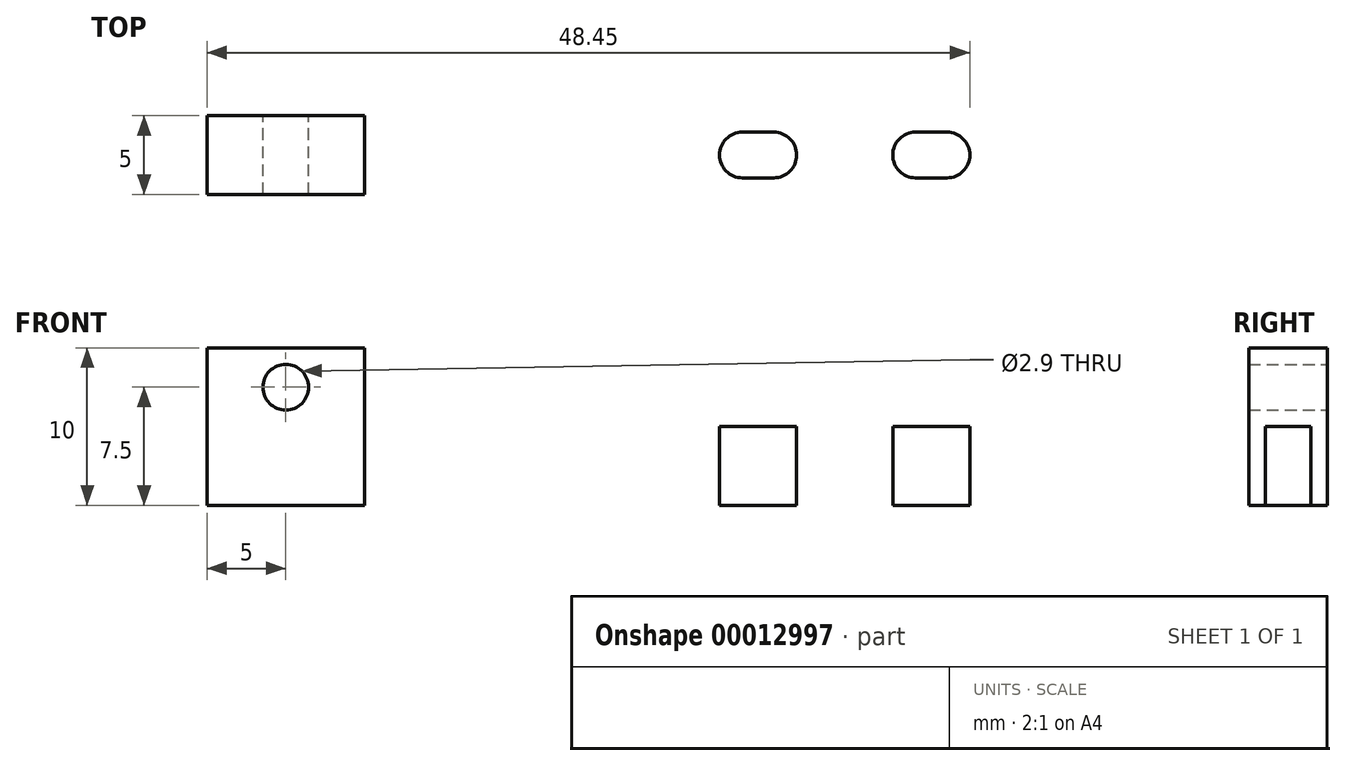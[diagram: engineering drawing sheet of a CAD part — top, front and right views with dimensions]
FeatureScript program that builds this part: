
annotation { "Feature Type Name" : "Feature", "Feature Type Description" : "" }
export const myFeature = defineFeature(function(context is Context, id is Id, definition is map)
    precondition{}
    {
        {
            var Q0;
            Q0=qCreatedBy(makeId("Top.planeOp"),FACE);
            var sketch = newSketch(context, id + "F0", { "sketchPlane" : qUnion([Q0])});
            skLineSegment(sketch, "E0.top", {"start": v(0, 7) * mm, "end": v(50, 7) * mm});
            skLineSegment(sketch, "E0.left", {"start": v(0, 0) * mm, "end": v(0, 7) * mm});
            skLineSegment(sketch, "E1", {"start": v(0, 0) * mm, "end": v(15, 0) * mm});
            skLineSegment(sketch, "E2", {"start": v(15, 0) * mm, "end": v(15, 2) * mm});
            skLineSegment(sketch, "E3", {"start": v(15, 2) * mm, "end": v(50, 2) * mm});
            skLineSegment(sketch, "E4", {"start": v(50, 2) * mm, "end": v(50, 7) * mm});
            skLineSegment(sketch, "E5.bottom", {"start": v(50, 7) * mm, "end": v(25, 7) * mm});
            skLineSegment(sketch, "E5.top", {"start": v(50, 9) * mm, "end": v(25, 9) * mm});
            skLineSegment(sketch, "E5.left", {"start": v(50, 7) * mm, "end": v(50, 9) * mm});
            skLineSegment(sketch, "E5.right", {"start": v(25, 7) * mm, "end": v(25, 9) * mm});
            skSolve(sketch);
        }
        {
            var Q0;
            Q0=makeQuery(id+"F0.imprint","IMPRINT",FACE,{"disambiguationData":[TD([[makeQuery(id+"F0.imprint","IMPRINT",EDGE,{"derivedFrom":sQuery(id+"F0.wireOp",EDGE,"E0.top")}),-1.0]])]});
            extrude(context, id + "F1", {"entities" : qUnion([Q0]), "depth" : 5 * mm});
        }
        {
            var Q0;
            Q0=makeQuery(id+"F1.opExtrude","CAP_FACE",FACE,{"disambiguationData":[OSD([sQuery(id+"F0.wireOp",EDGE,"E0.bottom"),sQuery(id+"F0.wireOp",EDGE,"E0.top"),sQuery(id+"F0.wireOp",EDGE,"E0.left"),sQuery(id+"F0.wireOp",EDGE,"E0.right")])],"isStart":false});
            var sketch = newSketch(context, id + "F2", { "sketchPlane" : qUnion([Q0])});
            skLineSegment(sketch, "E6.bottom", {"start": v(0, 7) * mm, "end": v(10, 7) * mm});
            skLineSegment(sketch, "E6.top", {"start": v(0, 2) * mm, "end": v(10, 2) * mm});
            skLineSegment(sketch, "E6.left", {"start": v(0, 7) * mm, "end": v(0, 2) * mm});
            skLineSegment(sketch, "E6.right", {"start": v(10, 7) * mm, "end": v(10, 2) * mm});
            skSolve(sketch);
        }
        {
            var Q0;
            Q0=makeQuery(id+"F2.imprint","IMPRINT",FACE,{"disambiguationData":[TD([[makeQuery(id+"F2.imprint","IMPRINT",EDGE,{"derivedFrom":sQuery(id+"F2.wireOp",EDGE,"E6.bottom")}),-1.0]])]});
            extrude(context, id + "F3", {"entities" : qUnion([Q0]), "operationType" : NewBodyOperationType.ADD, "depth" : 5 * mm});
        }
        {
            var Q0;
            Q0=makeQuery(id+"F3.boolean.opBoolean","MERGE",FACE,{"derivedFrom":[makeQuery(id+"F1.opExtrude","SWEPT_FACE",FACE,{"disambiguationData":[OSD([sQuery(id+"F0.wireOp",EDGE,"E0.top")])]}),makeQuery(id+"F3.opExtrude","SWEPT_FACE",FACE,{"disambiguationData":[OSD([sQuery(id+"F2.wireOp",EDGE,"E6.bottom")])]})]});
            var sketch = newSketch(context, id + "F4", { "sketchPlane" : qUnion([Q0])});
            skPoint(sketch, "E7", {"position": v(-5, 7.5) * mm});
            skSolve(sketch);
        }
        {
            var Q0;
            Q0=sQuery(id+"F4.wireOp",VERTEX,"E7");
            var Q1;
            Q1=makeQuery(id+"F1.opExtrude","SWEPT_BODY",BODY,{"disambiguationData":[OSD([sQuery(id+"F0.wireOp",EDGE,"E0.top"),sQuery(id+"F0.wireOp",EDGE,"E0.left"),sQuery(id+"F0.wireOp",EDGE,"E1"),sQuery(id+"F0.wireOp",EDGE,"E2"),sQuery(id+"F0.wireOp",EDGE,"E3"),sQuery(id+"F0.wireOp",EDGE,"E4")])]});
            hole(context, id + "F5", {"style" : HoleStyle.SIMPLE, "holeDiameter" : 2.9 * mm, "endStyle" : HoleEndStyle.THROUGH, "locations" : qUnion([Q0]), "scope" : qUnion([Q1])});
        }
        {
            var Q0;
            Q0=makeQuery(id+"F1.opExtrude","CAP_FACE",FACE,{"disambiguationData":[OSD([sQuery(id+"F0.wireOp",EDGE,"E0.top"),sQuery(id+"F0.wireOp",EDGE,"E0.left"),sQuery(id+"F0.wireOp",EDGE,"E1"),sQuery(id+"F0.wireOp",EDGE,"E2"),sQuery(id+"F0.wireOp",EDGE,"E3"),sQuery(id+"F0.wireOp",EDGE,"E4")])],"isStart":false});
            var sketch = newSketch(context, id + "F6", { "sketchPlane" : qUnion([Q0])});
            skLineSegment(sketch, "E8", {"start": v(45, 4.5) * mm, "end": v(47, 4.5) * mm});
            skLineSegment(sketch, "E9", {"start": v(34, 4.5) * mm, "end": v(36, 4.5) * mm});
            skArc(sketch, "E10.0.startCap", {"start": v(45, 3.05) * mm, "mid": v(43.55, 4.5) * mm, "end": v(45, 5.95) * mm});
            skArc(sketch, "E10.0.endCap", {"start": v(47, 5.95) * mm, "mid": v(48.45, 4.5) * mm, "end": v(47, 3.05) * mm});
            skLineSegment(sketch, "E10.0.left", {"start": v(45, 5.95) * mm, "end": v(47, 5.95) * mm});
            skLineSegment(sketch, "E10.0.right", {"start": v(45, 3.05) * mm, "end": v(47, 3.05) * mm});
            skArc(sketch, "E11.0.startCap", {"start": v(34, 3.05) * mm, "mid": v(32.55, 4.5) * mm, "end": v(34, 5.95) * mm});
            skArc(sketch, "E11.0.endCap", {"start": v(36, 5.95) * mm, "mid": v(37.45, 4.5) * mm, "end": v(36, 3.05) * mm});
            skLineSegment(sketch, "E11.0.left", {"start": v(34, 5.95) * mm, "end": v(36, 5.95) * mm});
            skLineSegment(sketch, "E11.0.right", {"start": v(34, 3.05) * mm, "end": v(36, 3.05) * mm});
            skSolve(sketch);
        }
        {
            var Q0;
            Q0=makeQuery(id+"F6.imprint","IMPRINT",FACE,{"disambiguationData":[TD([[makeQuery(id+"F6.imprint","IMPRINT",EDGE,{"derivedFrom":sQuery(id+"F6.wireOp",EDGE,"E11.0.startCap")}),-1.0]])]});
            var Q1;
            Q1=makeQuery(id+"F6.imprint","IMPRINT",FACE,{"disambiguationData":[TD([[makeQuery(id+"F6.imprint","IMPRINT",EDGE,{"derivedFrom":sQuery(id+"F6.wireOp",EDGE,"E10.0.startCap")}),-1.0]])]});
            extrude(context, id + "F7", {"entities" : qUnion([Q0, Q1]), "operationType" : NewBodyOperationType.REMOVE, "endBound" : BoundingType.THROUGH_ALL, "oppositeDirection" : true, "depth" : 25 * mm});
        }
    });
